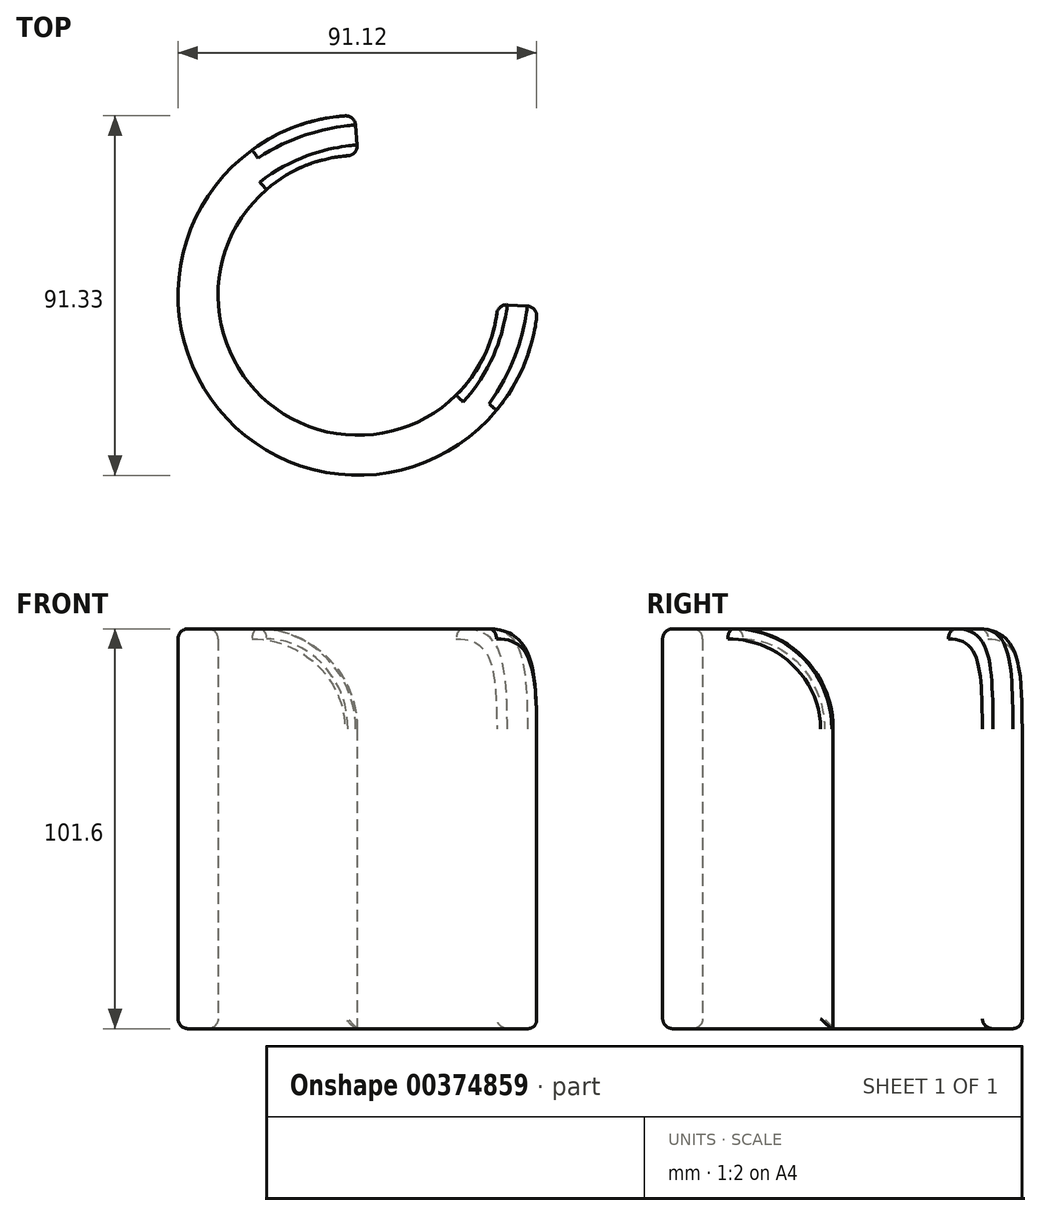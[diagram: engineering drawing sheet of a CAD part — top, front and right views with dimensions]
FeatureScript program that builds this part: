
annotation { "Feature Type Name" : "Feature", "Feature Type Description" : "" }
export const myFeature = defineFeature(function(context is Context, id is Id, definition is map)
    precondition{}
    {
        {
            var Q0;
            Q0=qCreatedBy(makeId("Top.planeOp"),FACE);
            var sketch = newSketch(context, id + "F0", { "sketchPlane" : qUnion([Q0])});
            skArc(sketch, "E0", {"start": v(0, 35.56) * mm, "mid": v(-25.93, -24.33) * mm, "end": v(35.49, -2.26) * mm});
            skArc(sketch, "E1.0", {"start": v(-0.8, 45.71) * mm, "mid": v(-33.06, -31.58) * mm, "end": v(45.63, -2.9) * mm});
            skLineSegment(sketch, "E2", {"start": v(0, 35.56) * mm, "end": v(-0.8, 45.71) * mm});
            skLineSegment(sketch, "E3", {"start": v(35.49, -2.26) * mm, "end": v(45.63, -2.9) * mm});
            skSolve(sketch);
        }
        {
            var Q0;
            Q0=makeQuery(id+"F0.imprint","IMPRINT",FACE,{"disambiguationData":[TD([[makeQuery(id+"F0.imprint","IMPRINT",EDGE,{"derivedFrom":sQuery(id+"F0.wireOp",EDGE,"E0")}),-1.0]])]});
            extrude(context, id + "F1", {"entities" : qUnion([Q0]), "depth" : 101.6 * mm});
        }
        {
            var Q0;
            Q0=makeQuery(id+"F1.opExtrude","CAP_EDGE",EDGE,{"disambiguationData":[OSD([sQuery(id+"F0.wireOp",EDGE,"E3")])],"isStart":false});
            var Q1;
            Q1=makeQuery(id+"F1.opExtrude","CAP_EDGE",EDGE,{"disambiguationData":[OSD([sQuery(id+"F0.wireOp",EDGE,"E2")])],"isStart":false});
            fillet(context, id + "F2", {"entities" : qUnion([Q0, Q1]), "radius" : 25.4 * mm, "tangentPropagation" : true, "allowEdgeOverflow" : false});
        }
        {
            var Q0;
            Q0=makeQuery(id+"F1.opExtrude","SWEPT_FACE",FACE,{"disambiguationData":[OSD([sQuery(id+"F0.wireOp",EDGE,"E0")])]});
            var Q1;
            Q1=makeQuery(id+"F1.opExtrude","SWEPT_FACE",FACE,{"disambiguationData":[OSD([sQuery(id+"F0.wireOp",EDGE,"E1.0")])]});
            fillet(context, id + "F3", {"entities" : qUnion([Q0, Q1]), "radius" : 2.54 * mm, "tangentPropagation" : true, "allowEdgeOverflow" : false});
        }
    });
